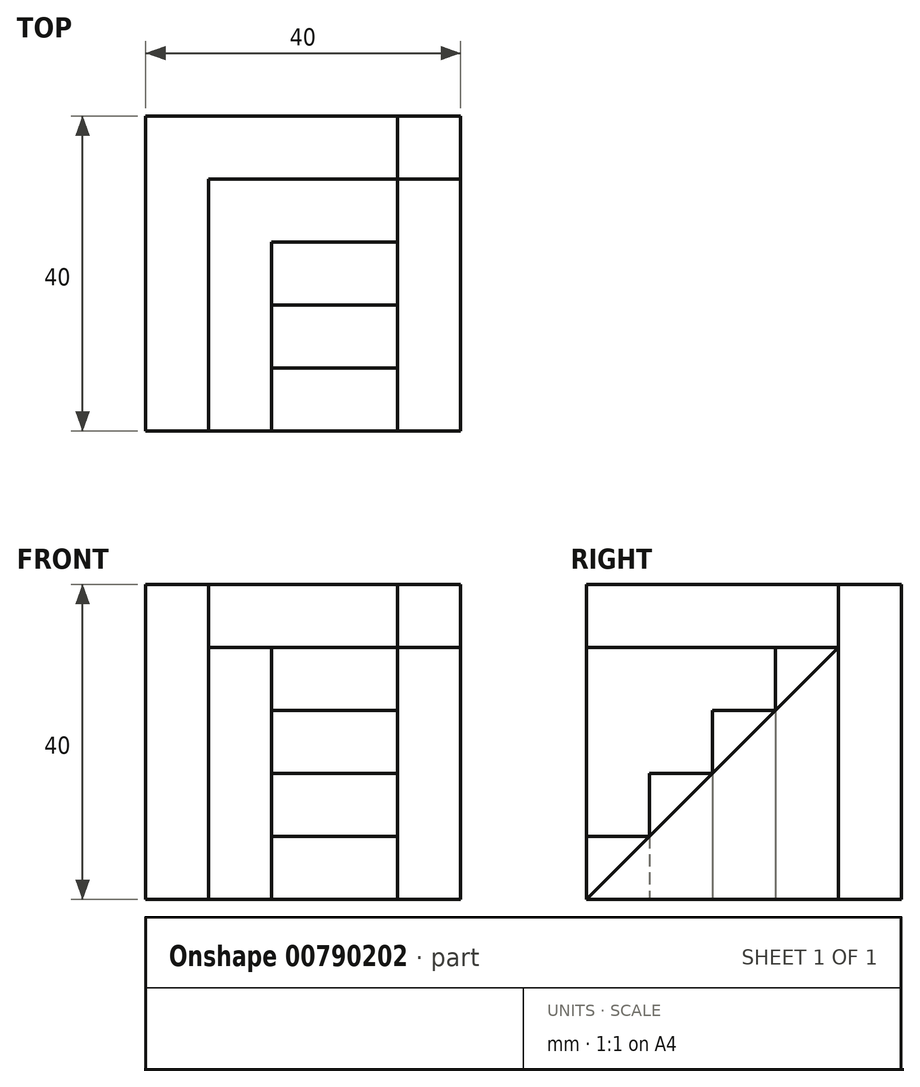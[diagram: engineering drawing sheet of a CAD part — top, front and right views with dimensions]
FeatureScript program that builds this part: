
annotation { "Feature Type Name" : "Feature", "Feature Type Description" : "" }
export const myFeature = defineFeature(function(context is Context, id is Id, definition is map)
    precondition{}
    {
        {
            var Q0;
            Q0=qCreatedBy(makeId("Top.planeOp"),FACE);
            var sketch = newSketch(context, id + "F0", { "sketchPlane" : qUnion([Q0])});
            skLineSegment(sketch, "E0.bottom", {"start": v(-20, 20) * mm, "end": v(20, 20) * mm});
            skLineSegment(sketch, "E0.top", {"start": v(-20, -20) * mm, "end": v(20, -20) * mm});
            skLineSegment(sketch, "E0.left", {"start": v(-20, 20) * mm, "end": v(-20, -20) * mm});
            skLineSegment(sketch, "E0.right", {"start": v(20, 20) * mm, "end": v(20, -20) * mm});
            skPoint(sketch, "E0.middle", {"position": v(0, 0) * mm});
            skLineSegment(sketch, "E1", {"start": v(-12, 12) * mm, "end": v(-12, -20) * mm});
            skLineSegment(sketch, "E2", {"start": v(12, 20) * mm, "end": v(12, -20) * mm});
            skLineSegment(sketch, "E3", {"start": v(-12, 12) * mm, "end": v(20, 12) * mm});
            skLineSegment(sketch, "E4", {"start": v(-4, -12) * mm, "end": v(12, -12) * mm});
            skLineSegment(sketch, "E5", {"start": v(-4, -20) * mm, "end": v(-4, 4) * mm});
            skLineSegment(sketch, "E6", {"start": v(12, -4) * mm, "end": v(-4, -4) * mm});
            skLineSegment(sketch, "E7", {"start": v(-4, 4) * mm, "end": v(12, 4) * mm});
            skPoint(sketch, "E8.orphan", {"position": v(-12, 20) * mm});
            skPoint(sketch, "E9.orphan", {"position": v(20, 4) * mm});
            skPoint(sketch, "E10.orphan", {"position": v(20, -4) * mm});
            skPoint(sketch, "E11.orphan", {"position": v(20, -12) * mm});
            skSolve(sketch);
        }
        {
            var Q0;
            {var subQ5=sQuery(id+"F0.wireOp",EDGE,"E0.right");var subQ6=sQuery(id+"F0.wireOp",EDGE,"E0.top");var subQ7=makeQuery(id+"F0.imprint","INTERSECT",VERTEX,{"derivedFrom":[subQ6,subQ5]});Q0=makeQuery(id+"F0.imprint","IMPRINT",FACE,{"disambiguationData":[TD([[makeQuery(id+"F0.imprint","IMPRINT",EDGE,{"disambiguationData":[TD([[subQ7,1.0]])],"derivedFrom":subQ6}),1.0]])]});}
            extrude(context, id + "F1", {"entities" : qUnion([Q0]), "depth" : 32 * mm, "offsetDistance" : 25 * mm});
        }
        {
            var Q0;
            Q0=makeQuery(id+"F1.opExtrude","SWEPT_FACE",FACE,{"disambiguationData":[OSD([sQuery(id+"F0.wireOp",EDGE,"E0.right")])]});
            var sketch = newSketch(context, id + "F2", { "sketchPlane" : qUnion([Q0])});
            skLineSegment(sketch, "E12", {"start": v(12, 32) * mm, "end": v(-20, 0) * mm});
            skSolve(sketch);
        }
        {
            var Q0;
            Q0=makeQuery(id+"F2.imprint","IMPRINT",FACE,{"disambiguationData":[TD([[makeQuery(id+"F2.imprint","IMPRINT",EDGE,{"derivedFrom":sQuery(id+"F2.wireOp",EDGE,"E12")}),-1.0]])]});
            extrude(context, id + "F3", {"entities" : qUnion([Q0]), "operationType" : NewBodyOperationType.REMOVE, "oppositeDirection" : true, "depth" : 25 * mm, "offsetDistance" : 25 * mm});
        }
        {
            var Q0;
            {var subQ1=sQuery(id+"F0.wireOp",EDGE,"E0.left");Q0=makeQuery(id+"F0.imprint","IMPRINT",FACE,{"disambiguationData":[TD([[makeQuery(id+"F0.imprint","IMPRINT",EDGE,{"derivedFrom":subQ1}),1.0]])]});}
            extrude(context, id + "F4", {"entities" : qUnion([Q0]), "depth" : 40 * mm, "offsetDistance" : 25 * mm});
        }
        {
            var Q0;
            {var subQ0=sQuery(id+"F0.wireOp",EDGE,"E0.right");var subQ1=sQuery(id+"F0.wireOp",EDGE,"E0.bottom");var subQ2=makeQuery(id+"F0.imprint","INTERSECT",VERTEX,{"derivedFrom":[subQ1,subQ0]});Q0=makeQuery(id+"F0.imprint","IMPRINT",FACE,{"disambiguationData":[TD([[makeQuery(id+"F0.imprint","IMPRINT",EDGE,{"disambiguationData":[TD([[subQ2,1.0]])],"derivedFrom":subQ1}),-1.0]])]});}
            extrude(context, id + "F5", {"entities" : qUnion([Q0]), "depth" : 40 * mm, "offsetDistance" : 25 * mm});
        }
        {
            var Q0;
            {var subQ1=sQuery(id+"F0.wireOp",EDGE,"E1");Q0=makeQuery(id+"F0.imprint","IMPRINT",FACE,{"disambiguationData":[TD([[makeQuery(id+"F0.imprint","IMPRINT",EDGE,{"derivedFrom":subQ1}),1.0]])]});}
            extrude(context, id + "F6", {"entities" : qUnion([Q0]), "depth" : 32 * mm, "offsetDistance" : 25 * mm});
        }
        {
            var Q0;
            {var subQ0=sQuery(id+"F0.wireOp",EDGE,"E6");Q0=makeQuery(id+"F0.imprint","IMPRINT",FACE,{"disambiguationData":[TD([[makeQuery(id+"F0.imprint","IMPRINT",EDGE,{"derivedFrom":subQ0}),-1.0]])]});}
            extrude(context, id + "F7", {"entities" : qUnion([Q0]), "depth" : 24 * mm, "offsetDistance" : 25 * mm});
        }
        {
            var Q0;
            {var subQ0=sQuery(id+"F0.wireOp",EDGE,"E4");Q0=makeQuery(id+"F0.imprint","IMPRINT",FACE,{"disambiguationData":[TD([[makeQuery(id+"F0.imprint","IMPRINT",EDGE,{"derivedFrom":subQ0}),1.0]])]});}
            extrude(context, id + "F8", {"entities" : qUnion([Q0]), "depth" : 16 * mm, "offsetDistance" : 25 * mm});
        }
        {
            var Q0;
            {var subQ5=sQuery(id+"F0.wireOp",EDGE,"E4");Q0=makeQuery(id+"F0.imprint","IMPRINT",FACE,{"disambiguationData":[TD([[makeQuery(id+"F0.imprint","IMPRINT",EDGE,{"derivedFrom":subQ5}),-1.0]])]});}
            extrude(context, id + "F9", {"entities" : qUnion([Q0]), "depth" : 8 * mm, "offsetDistance" : 25 * mm});
        }
    });
